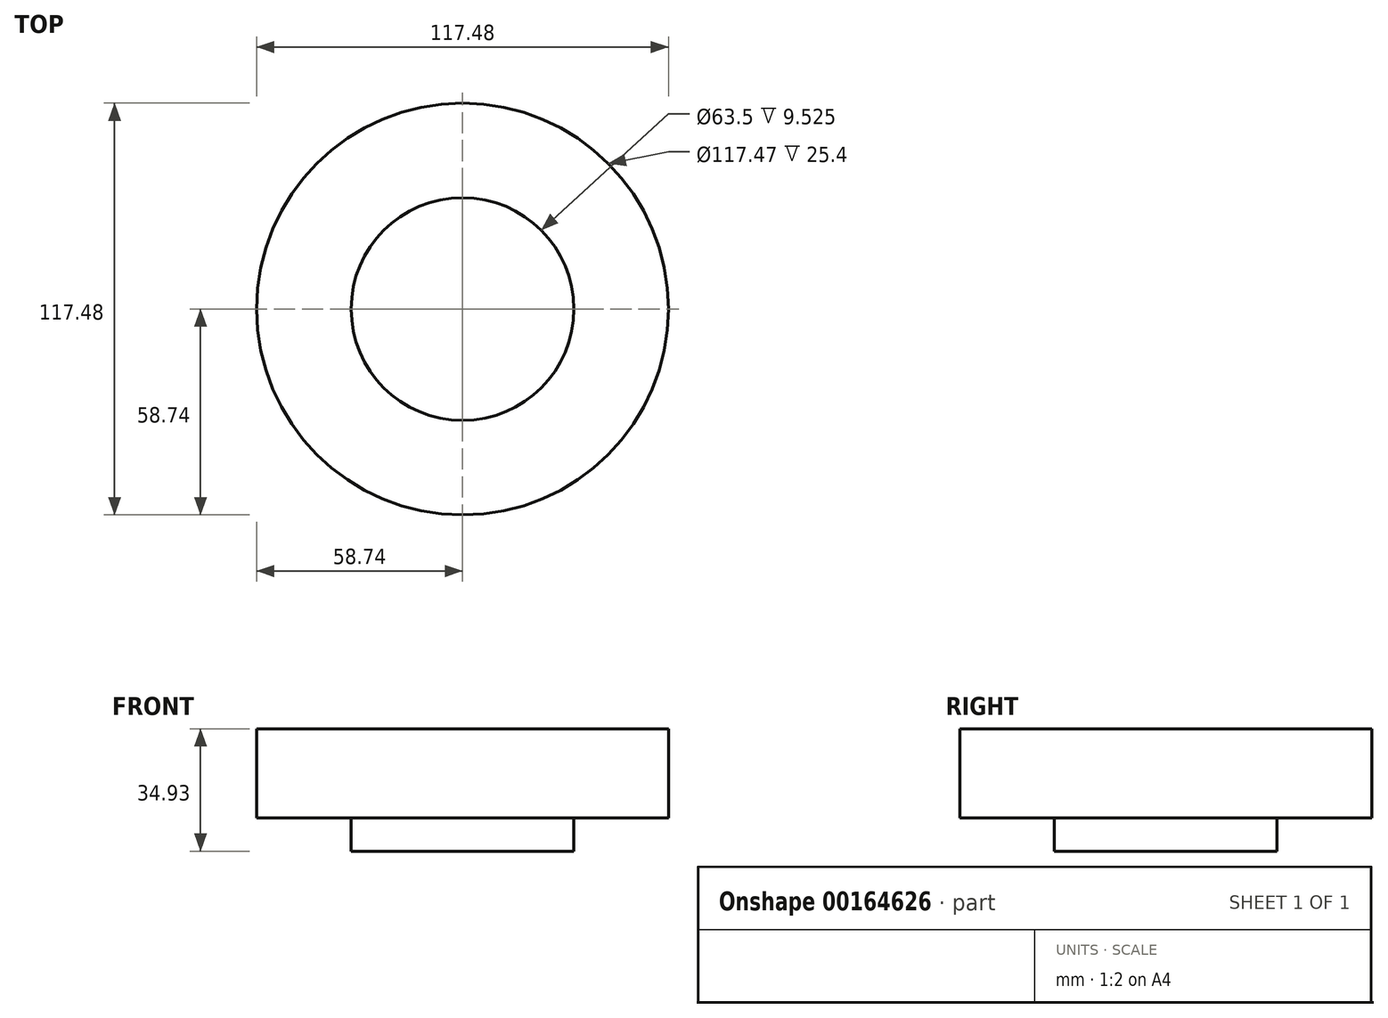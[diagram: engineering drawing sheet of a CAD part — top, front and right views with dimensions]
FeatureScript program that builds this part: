
annotation { "Feature Type Name" : "Feature", "Feature Type Description" : "" }
export const myFeature = defineFeature(function(context is Context, id is Id, definition is map)
    precondition{}
    {
        {
            var Q0;
            Q0=qCreatedBy(makeId("Front.planeOp"),FACE);
            var sketch = newSketch(context, id + "F0", { "sketchPlane" : qUnion([Q0])});
            skLineSegment(sketch, "E0", {"start": v(-58.74, 60.32) * mm, "end": v(0, 60.33) * mm});
            skLineSegment(sketch, "E1", {"start": v(-58.74, 60.32) * mm, "end": v(-58.74, 34.92) * mm});
            skLineSegment(sketch, "E2", {"start": v(-58.74, 34.92) * mm, "end": v(-31.75, 34.92) * mm});
            skLineSegment(sketch, "E3", {"start": v(-31.75, 34.92) * mm, "end": v(-31.75, 25.4) * mm});
            skLineSegment(sketch, "E4", {"start": v(-31.75, 25.4) * mm, "end": v(0, 25.4) * mm});
            skLineSegment(sketch, "E5", {"start": v(0, 72.17) * mm, "end": v(0, -34.41) * mm, "construction": true});
            skSolve(sketch);
        }
        {
            var Q0;
            Q0 = qSketchRegion(id + "F0", true);
            var Q1;
            Q1=sQuery(id+"F0.wireOp",EDGE,"E0");
            var Q2;
            Q2=sQuery(id+"F0.wireOp",EDGE,"E2");
            var Q3;
            Q3=sQuery(id+"F0.wireOp",EDGE,"E1");
            var Q4;
            Q4=sQuery(id+"F0.wireOp",EDGE,"E4");
            var Q5;
            Q5=sQuery(id+"F0.wireOp",EDGE,"E3");
            var Q6;
            Q6=sQuery(id+"F0.wireOp",EDGE,"E5");
            revolve(context, id + "F1", {"bodyType" : ToolBodyType.SURFACE, "entities" : qUnion([Q0]), "surfaceEntities" : qUnion([Q1, Q2, Q3, Q4, Q5]), "axis" : qUnion([Q6]), "revolveType" : RevolveType.FULL});
        }
    });
